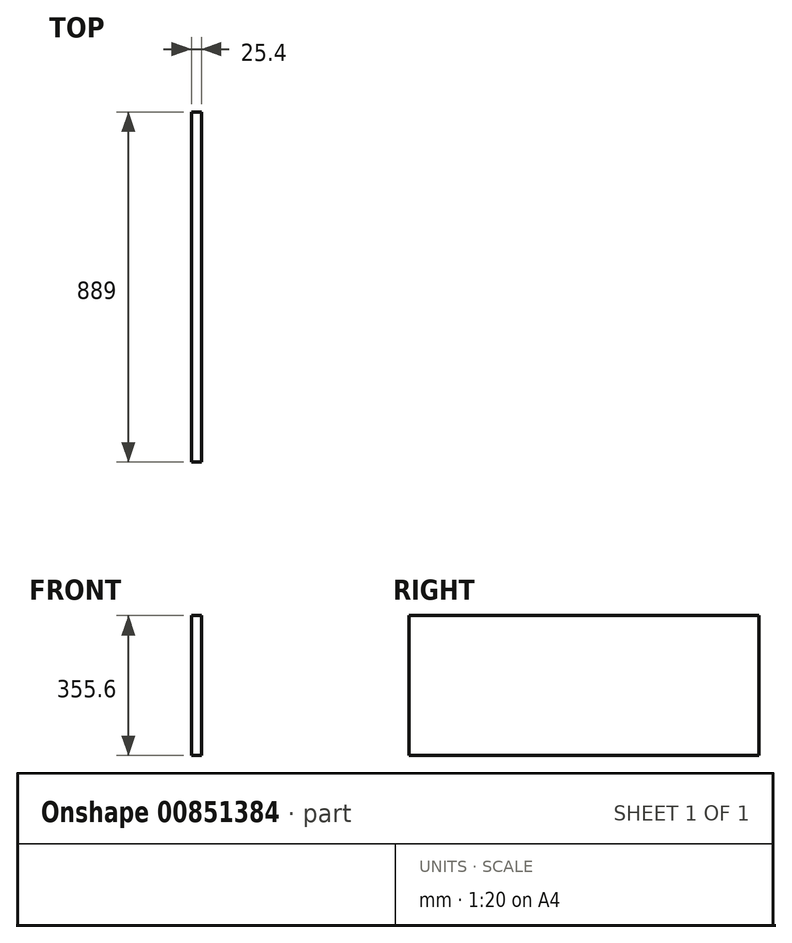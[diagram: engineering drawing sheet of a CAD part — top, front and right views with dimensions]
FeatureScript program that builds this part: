
annotation { "Feature Type Name" : "Feature", "Feature Type Description" : "" }
export const myFeature = defineFeature(function(context is Context, id is Id, definition is map)
    precondition{}
    {
        {
            var Q0;
            Q0=qCreatedBy(makeId("Front.planeOp"),FACE);
            var sketch = newSketch(context, id + "F0", { "sketchPlane" : qUnion([Q0])});
            skLineSegment(sketch, "E0.bottom", {"start": v(-31, 289.15) * mm, "end": v(-5.6, 289.15) * mm});
            skLineSegment(sketch, "E0.top", {"start": v(-31, -66.45) * mm, "end": v(-5.6, -66.45) * mm});
            skLineSegment(sketch, "E0.left", {"start": v(-31, 289.15) * mm, "end": v(-31, -66.45) * mm});
            skLineSegment(sketch, "E0.right", {"start": v(-5.6, 289.15) * mm, "end": v(-5.6, -66.45) * mm});
            skSolve(sketch);
        }
        {
            var Q0;
            Q0 = qSketchRegion(id + "F0", true);
            extrude(context, id + "F1", {"entities" : qUnion([Q0]), "depth" : 889 * mm, "offsetDistance" : 25.4 * mm});
        }
    });
